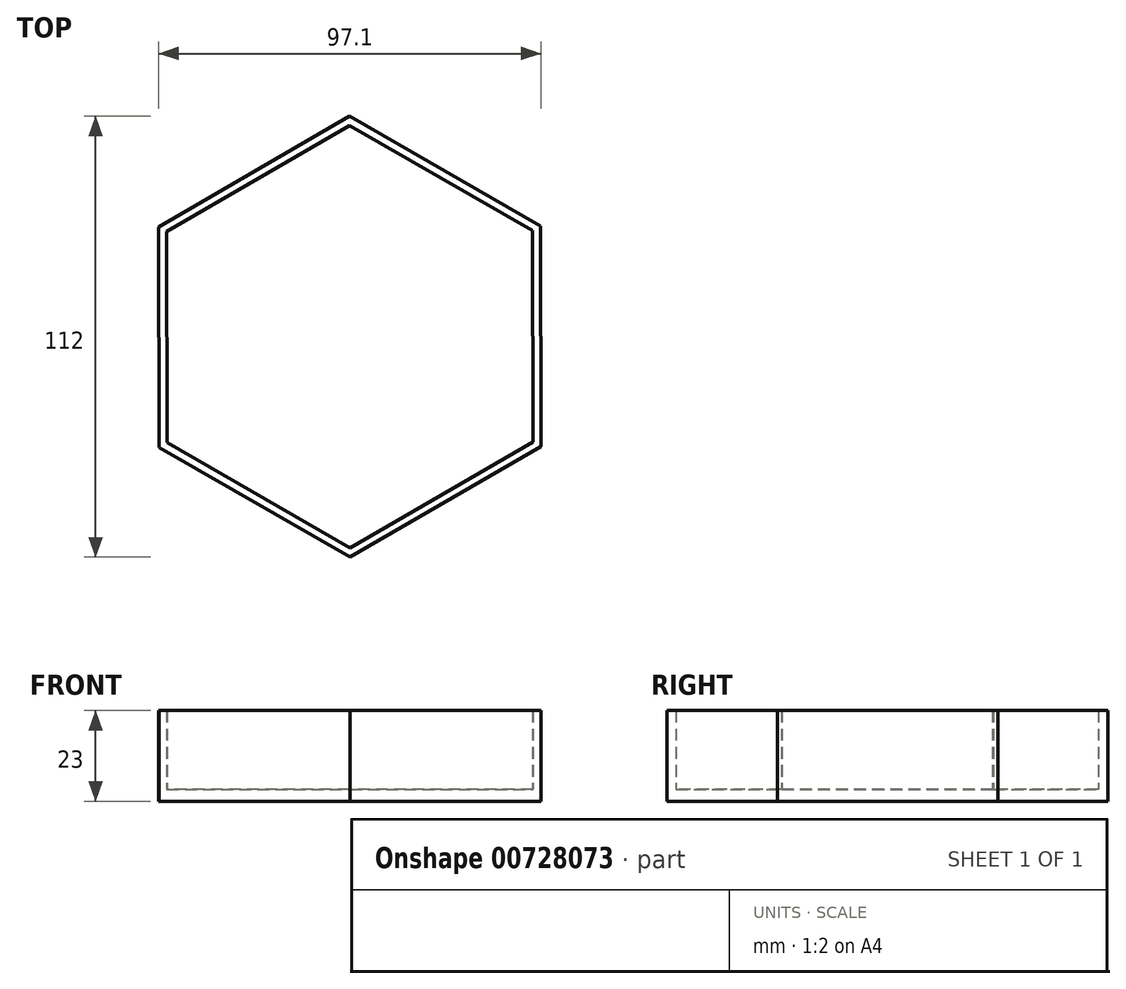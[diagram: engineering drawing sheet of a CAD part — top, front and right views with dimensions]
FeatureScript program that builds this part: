
annotation { "Feature Type Name" : "Feature", "Feature Type Description" : "" }
export const myFeature = defineFeature(function(context is Context, id is Id, definition is map)
    precondition{}
    {
        {
            var Q0;
            Q0=qCreatedBy(makeId("Top.planeOp"),FACE);
            var sketch = newSketch(context, id + "F0", { "sketchPlane" : qUnion([Q0])});
            skCircle(sketch, "E0.cCircle", {"center": v(0, 0) * mm, "radius": 48.5 * mm, "construction": true});
            skLineSegment(sketch, "E0.0", {"start": v(-0.1, 56) * mm, "end": v(48.45, 28.09) * mm});
            skLineSegment(sketch, "E0.1", {"start": v(48.45, 28.09) * mm, "end": v(48.55, -27.91) * mm});
            skLineSegment(sketch, "E0.2", {"start": v(48.55, -27.91) * mm, "end": v(0.1, -56) * mm});
            skLineSegment(sketch, "E0.3", {"start": v(0.1, -56) * mm, "end": v(-48.45, -28.09) * mm});
            skLineSegment(sketch, "E0.4", {"start": v(-48.45, -28.09) * mm, "end": v(-48.55, 27.91) * mm});
            skLineSegment(sketch, "E0.5", {"start": v(-48.55, 27.91) * mm, "end": v(-0.1, 56) * mm});
            skPoint(sketch, "E0.0.midPoint", {"position": v(24.17, 42.05) * mm});
            skPoint(sketch, "E1.0.midPoint", {"position": v(25.21, 43.85) * mm});
            skSolve(sketch);
        }
        {
            var Q0;
            Q0=makeQuery(id+"F0.imprint","IMPRINT",FACE,{"disambiguationData":[TD([[makeQuery(id+"F0.imprint","IMPRINT",EDGE,{"derivedFrom":sQuery(id+"F0.wireOp",EDGE,"E0.0")}),-1.0]])]});
            extrude(context, id + "F1", {"entities" : qUnion([Q0]), "depth" : 3 * mm, "offsetDistance" : 25 * mm});
        }
        {
            var Q0;
            Q0=makeQuery(id+"F1.opExtrude","CAP_FACE",FACE,{"disambiguationData":[OSD([sQuery(id+"F0.wireOp",EDGE,"E0.0"),sQuery(id+"F0.wireOp",EDGE,"E0.1"),sQuery(id+"F0.wireOp",EDGE,"E0.2"),sQuery(id+"F0.wireOp",EDGE,"E0.3"),sQuery(id+"F0.wireOp",EDGE,"E0.4"),sQuery(id+"F0.wireOp",EDGE,"E0.5")])],"isStart":false});
            var sketch = newSketch(context, id + "F2", { "sketchPlane" : qUnion([Q0])});
            skLineSegment(sketch, "E2.0", {"start": v(46.45, 26.93) * mm, "end": v(-0.1, 53.7) * mm});
            skLineSegment(sketch, "E2.1", {"start": v(-46.55, 26.76) * mm, "end": v(-46.45, -26.93) * mm});
            skLineSegment(sketch, "E2.2", {"start": v(-46.45, -26.93) * mm, "end": v(0.1, -53.7) * mm});
            skLineSegment(sketch, "E2.3", {"start": v(-0.1, 53.7) * mm, "end": v(-46.55, 26.76) * mm});
            skLineSegment(sketch, "E2.4", {"start": v(0.1, -53.7) * mm, "end": v(46.55, -26.76) * mm});
            skLineSegment(sketch, "E2.5", {"start": v(46.55, -26.76) * mm, "end": v(46.45, 26.93) * mm});
            skSolve(sketch);
        }
        {
            var Q0;
            Q0=makeQuery(id+"F2.imprint","IMPRINT",FACE,{"disambiguationData":[TD([[makeQuery(id+"F2.imprint","IMPRINT",EDGE,{"derivedFrom":sQuery(id+"F2.wireOp",EDGE,"E2.0")}),-1.0]])]});
            extrude(context, id + "F3", {"entities" : qUnion([Q0]), "operationType" : NewBodyOperationType.ADD, "depth" : 20 * mm, "offsetDistance" : 25 * mm});
        }
    });
